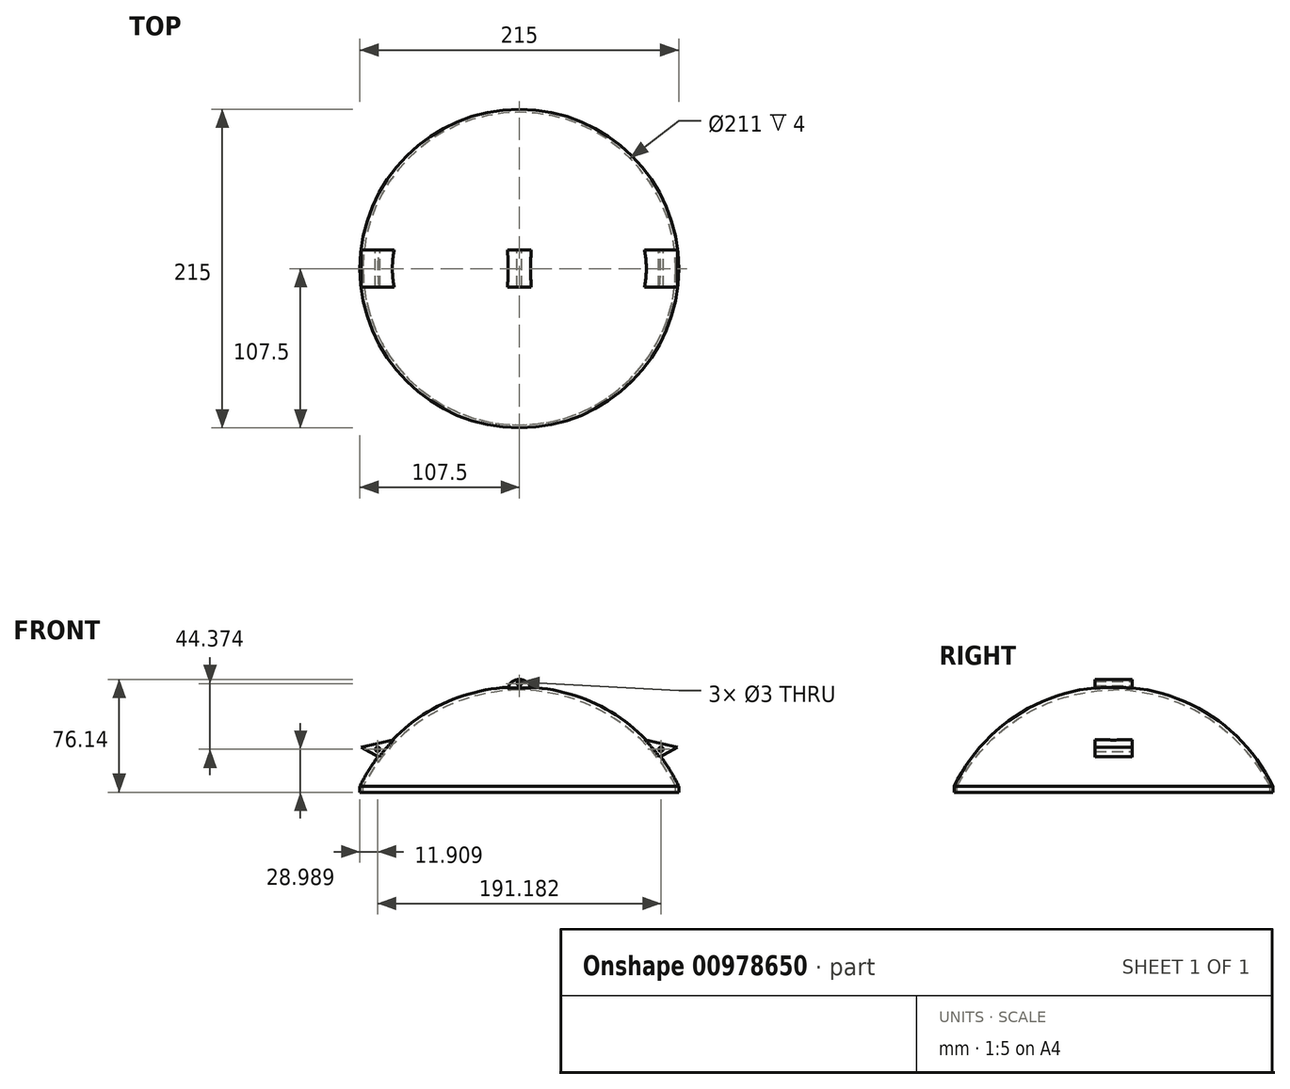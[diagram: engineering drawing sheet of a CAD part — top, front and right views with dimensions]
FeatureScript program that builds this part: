
annotation { "Feature Type Name" : "Feature", "Feature Type Description" : "" }
export const myFeature = defineFeature(function(context is Context, id is Id, definition is map)
    precondition{}
    {
        {
            var Q0;
            Q0=qCreatedBy(makeId("Front.planeOp"),FACE);
            var sketch = newSketch(context, id + "F0", { "sketchPlane" : qUnion([Q0])});
            skLineSegment(sketch, "E0", {"start": v(0, 0) * mm, "end": v(-107.5, 0) * mm});
            skLineSegment(sketch, "E1", {"start": v(0, 0) * mm, "end": v(0, 67) * mm});
            skArc(sketch, "E2", {"start": v(0, 67) * mm, "mid": v(-63.47, 49.1) * mm, "end": v(-107.5, 0) * mm});
            skSolve(sketch);
        }
        {
            var Q0;
            Q0=qCreatedBy(makeId("Front.planeOp"),FACE);
            var sketch = newSketch(context, id + "F1", { "sketchPlane" : qUnion([Q0])});
            skLineSegment(sketch, "E3", {"start": v(0, 0) * mm, "end": v(-105.5, 0) * mm});
            skLineSegment(sketch, "E4", {"start": v(0, 0) * mm, "end": v(0, 65) * mm});
            skArc(sketch, "E5", {"start": v(0, 65) * mm, "mid": v(-61.79, 47.17) * mm, "end": v(-105.5, 0) * mm});
            skSolve(sketch);
        }
        {
            var Q0;
            Q0 = qSketchRegion(id + "F0", true);
            var Q1;
            Q1=sQuery(id+"F0.wireOp",EDGE,"E1");
            revolve(context, id + "F2", {"surfaceOperationType" : NewSurfaceOperationType.NEW, "entities" : qUnion([Q0]), "axis" : qUnion([Q1]), "revolveType" : RevolveType.FULL});
        }
        {
            var Q0;
            Q0 = qSketchRegion(id + "F1", true);
            var Q1;
            Q1=sQuery(id+"F1.wireOp",EDGE,"E4");
            revolve(context, id + "F3", {"operationType" : NewBodyOperationType.REMOVE, "surfaceOperationType" : NewSurfaceOperationType.NEW, "entities" : qUnion([Q0]), "axis" : qUnion([Q1]), "revolveType" : RevolveType.FULL, "oppositeDirection" : true});
        }
        {
            var Q0;
            Q0=qCreatedBy(makeId("Front.planeOp"),FACE);
            var sketch = newSketch(context, id + "F4", { "sketchPlane" : qUnion([Q0])});
            skLineSegment(sketch, "E6.bottom", {"start": v(-105.5, 0) * mm, "end": v(-107.5, 0) * mm});
            skLineSegment(sketch, "E6.top", {"start": v(-105.5, -4) * mm, "end": v(-107.5, -4) * mm});
            skLineSegment(sketch, "E6.left", {"start": v(-105.5, 0) * mm, "end": v(-105.5, -4) * mm});
            skLineSegment(sketch, "E6.right", {"start": v(-107.5, 0) * mm, "end": v(-107.5, -4) * mm});
            skLineSegment(sketch, "E7", {"start": v(0, 0) * mm, "end": v(0, -6.13) * mm});
            skSolve(sketch);
        }
        {
            var Q0;
            Q0 = qSketchRegion(id + "F4", true);
            var Q1;
            Q1=sQuery(id+"F4.wireOp",EDGE,"E7");
            revolve(context, id + "F5", {"operationType" : NewBodyOperationType.ADD, "surfaceOperationType" : NewSurfaceOperationType.NEW, "entities" : qUnion([Q0]), "axis" : qUnion([Q1]), "revolveType" : RevolveType.FULL});
        }
        {
            var Q0;
            Q0=qCreatedBy(makeId("Front.planeOp"),FACE);
            var sketch = newSketch(context, id + "F6", { "sketchPlane" : qUnion([Q0])});
            skLineSegment(sketch, "E8", {"start": v(-93.44, 19.13) * mm, "end": v(-84.53, 31.51) * mm});
            skCircle(sketch, "E9", {"center": v(-95.6, 24.99) * mm, "radius": 1.5 * mm});
            skLineSegment(sketch, "E10", {"start": v(-93.44, 19.13) * mm, "end": v(-106.58, 26.37) * mm});
            skLineSegment(sketch, "E11", {"start": v(-106.58, 26.37) * mm, "end": v(-84.53, 31.51) * mm});
            skSolve(sketch);
        }
        {
            var Q0;
            Q0 = qSketchRegion(id + "F6", true);
            extrude(context, id + "F7", {"entities" : qUnion([Q0]), "operationType" : NewBodyOperationType.ADD, "endBound" : BoundingType.SYMMETRIC, "depth" : 25 * mm, "offsetDistance" : 25 * mm});
        }
        {
            var Q0;
            Q0=qCreatedBy(makeId("Front.planeOp"),FACE);
            var sketch = newSketch(context, id + "F8", { "sketchPlane" : qUnion([Q0])});
            skLineSegment(sketch, "E12.MirrorCS", {"start": v(93.44, 19.13) * mm, "end": v(106.58, 26.37) * mm});
            skLineSegment(sketch, "E13.MirrorCS", {"start": v(106.58, 26.37) * mm, "end": v(84.53, 31.51) * mm});
            skLineSegment(sketch, "E14.MirrorCS", {"start": v(93.44, 19.13) * mm, "end": v(84.53, 31.51) * mm});
            skCircle(sketch, "E15.MirrorC", {"center": v(95.6, 24.99) * mm, "radius": 1.5 * mm});
            skSolve(sketch);
        }
        {
            var Q0;
            Q0 = qSketchRegion(id + "F8", true);
            extrude(context, id + "F9", {"entities" : qUnion([Q0]), "operationType" : NewBodyOperationType.ADD, "endBound" : BoundingType.SYMMETRIC, "depth" : 25 * mm, "offsetDistance" : 25 * mm});
        }
        {
            var Q0;
            Q0=qCreatedBy(makeId("Front.planeOp"),FACE);
            var sketch = newSketch(context, id + "F10", { "sketchPlane" : qUnion([Q0])});
            skLineSegment(sketch, "E16", {"start": v(-8, 65.74) * mm, "end": v(8, 65.74) * mm});
            skArc(sketch, "E17", {"start": v(8, 65.74) * mm, "mid": v(0, 72.14) * mm, "end": v(-8, 65.74) * mm});
            skCircle(sketch, "E18", {"center": v(0, 69.36) * mm, "radius": 1.5 * mm});
            skSolve(sketch);
        }
        {
            var Q0;
            Q0 = qSketchRegion(id + "F10", true);
            extrude(context, id + "F11", {"entities" : qUnion([Q0]), "operationType" : NewBodyOperationType.ADD, "endBound" : BoundingType.SYMMETRIC, "depth" : 25 * mm, "offsetDistance" : 25 * mm});
        }
    });
